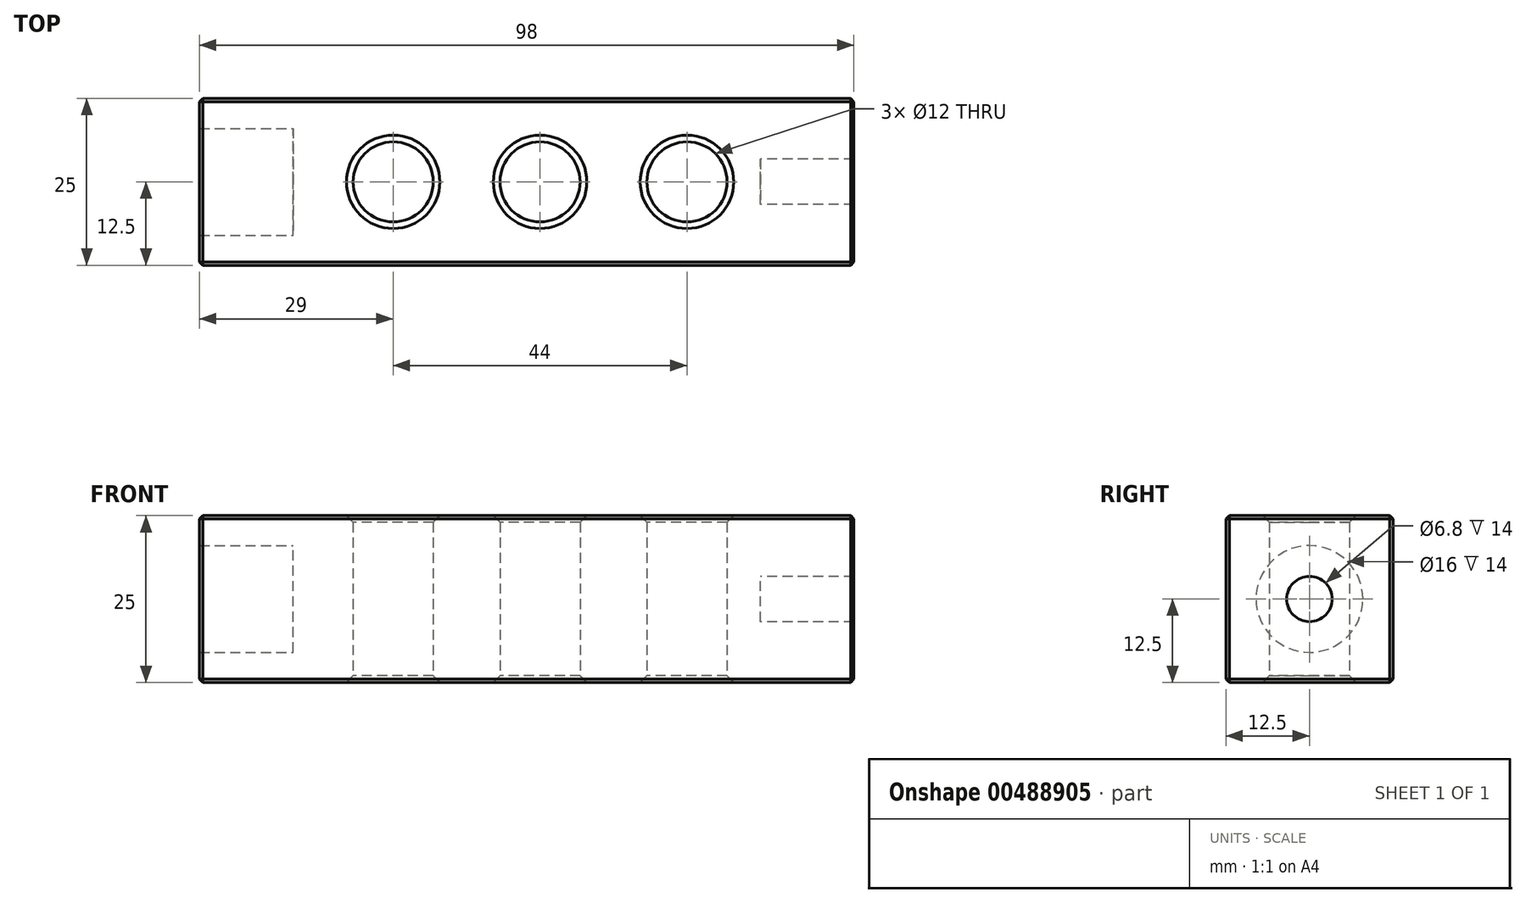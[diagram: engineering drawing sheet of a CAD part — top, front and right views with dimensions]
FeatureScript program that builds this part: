
annotation { "Feature Type Name" : "Feature", "Feature Type Description" : "" }
export const myFeature = defineFeature(function(context is Context, id is Id, definition is map)
    precondition{}
    {
        {
            var Q0;
            Q0=qCreatedBy(makeId("Top.planeOp"),FACE);
            var sketch = newSketch(context, id + "F0", { "sketchPlane" : qUnion([Q0])});
            skLineSegment(sketch, "E0.bottom", {"start": v(49, 12.5) * mm, "end": v(-49, 12.5) * mm});
            skLineSegment(sketch, "E0.top", {"start": v(49, -12.5) * mm, "end": v(-49, -12.5) * mm});
            skLineSegment(sketch, "E0.left", {"start": v(49, 12.5) * mm, "end": v(49, -12.5) * mm});
            skLineSegment(sketch, "E0.right", {"start": v(-49, 12.5) * mm, "end": v(-49, -12.5) * mm});
            skPoint(sketch, "E0.middle", {"position": v(0, 0) * mm});
            skLineSegment(sketch, "E1", {"start": v(49, 0) * mm, "end": v(-49, 0) * mm, "construction": true});
            skLineSegment(sketch, "E2", {"start": v(49, 12.5) * mm, "end": v(49, 22.83) * mm, "construction": true});
            skLineSegment(sketch, "E3", {"start": v(49, 22.83) * mm, "end": v(24, 22.83) * mm, "construction": true});
            skLineSegment(sketch, "E4", {"start": v(24, 22.83) * mm, "end": v(24, -3.88) * mm, "construction": true});
            skCircle(sketch, "E5", {"center": v(24, 0) * mm, "radius": 6 * mm});
            skCircle(sketch, "E6.1.0.0", {"center": v(2, 0) * mm, "radius": 6 * mm});
            skCircle(sketch, "E6.2.0.0", {"center": v(-20, 0) * mm, "radius": 6 * mm});
            skLineSegment(sketch, "E6.direction1", {"start": v(24, 0) * mm, "end": v(2, 0) * mm, "construction": true});
            skSolve(sketch);
        }
        {
            var Q0;
            Q0=makeQuery(id+"F0.imprint","IMPRINT",FACE,{"disambiguationData":[TD([[makeQuery(id+"F0.imprint","IMPRINT",EDGE,{"derivedFrom":sQuery(id+"F0.wireOp",EDGE,"E0.bottom")}),1.0]])]});
            extrude(context, id + "F1", {"entities" : qUnion([Q0]), "depth" : 25 * mm});
        }
        {
            var Q0;
            Q0=qCreatedBy(makeId("Right.planeOp"),FACE);
            var sketch = newSketch(context, id + "F2", { "sketchPlane" : qUnion([Q0])});
            skLineSegment(sketch, "E7", {"start": v(0, 0) * mm, "end": v(0, 12.5) * mm, "construction": true});
            skCircle(sketch, "E8", {"center": v(0, 12.5) * mm, "radius": 3.4 * mm});
            skSolve(sketch);
        }
        {
            var Q0;
            Q0 = qSketchRegion(id + "F2", true);
            extrude(context, id + "F3", {"entities" : qUnion([Q0]), "operationType" : NewBodyOperationType.REMOVE, "depth" : 120 * mm, "hasSecondDirection" : true, "secondDirectionOppositeDirection" : true, "secondDirectionDepth" : -35 * mm, "offsetDistance" : 25 * mm});
        }
        {
            var Q0;
            Q0=qCreatedBy(makeId("Top.planeOp"),FACE);
            cPlane(context, id + "F4", {"entities" : qUnion([Q0]), "cplaneType" : CPlaneType.OFFSET, "offset" : 12.5 * mm, "width" : 150 * mm, "height" : 150 * mm});
        }
        {
            var Q0;
            Q0=qCreatedBy(id+"F4.planeOp",FACE);
            var sketch = newSketch(context, id + "F5", { "sketchPlane" : qUnion([Q0])});
            skLineSegment(sketch, "E9", {"start": v(0, 0) * mm, "end": v(100, 0) * mm, "construction": true});
            skArc(sketch, "E10", {"start": v(112.5, 0) * mm, "mid": v(100, 12.5) * mm, "end": v(87.5, 0) * mm});
            skLineSegment(sketch, "E11", {"start": v(100, 0) * mm, "end": v(112.5, 0) * mm});
            skLineSegment(sketch, "E12", {"start": v(100, 0) * mm, "end": v(87.5, 0) * mm});
            skSolve(sketch);
        }
        {
            var Q0;
            Q0=qCreatedBy(makeId("Right.planeOp"),FACE);
            var sketch = newSketch(context, id + "F6", { "sketchPlane" : qUnion([Q0])});
            skLineSegment(sketch, "E13", {"start": v(0, 0) * mm, "end": v(0, 12.5) * mm, "construction": true});
            skCircle(sketch, "E14", {"center": v(0, 12.5) * mm, "radius": 8 * mm});
            skSolve(sketch);
        }
        {
            var Q0;
            Q0 = qSketchRegion(id + "F6", true);
            extrude(context, id + "F7", {"entities" : qUnion([Q0]), "operationType" : NewBodyOperationType.REMOVE, "oppositeDirection" : true, "depth" : 100 * mm, "hasSecondDirection" : true, "secondDirectionOppositeDirection" : true, "secondDirectionDepth" : 35 * mm, "offsetDistance" : 25 * mm});
        }
        {
            var Q0;
            Q0=makeQuery(id+"F1.opExtrude","SWEPT_EDGE",EDGE,{"disambiguationData":[OSD([sQuery(id+"F0.wireOp",EDGE,"E0.bottom"),sQuery(id+"F0.wireOp",EDGE,"E0.left")])]});
            var Q1;
            Q1=makeQuery(id+"F1.opExtrude","SWEPT_EDGE",EDGE,{"disambiguationData":[OSD([sQuery(id+"F0.wireOp",EDGE,"E0.top"),sQuery(id+"F0.wireOp",EDGE,"E0.left")])]});
            var Q2;
            Q2=makeQuery(id+"F1.opExtrude","CAP_EDGE",EDGE,{"disambiguationData":[OSD([sQuery(id+"F0.wireOp",EDGE,"E0.left")])],"isStart":true});
            var Q3;
            Q3=makeQuery(id+"F1.opExtrude","CAP_EDGE",EDGE,{"disambiguationData":[OSD([sQuery(id+"F0.wireOp",EDGE,"E0.left")])],"isStart":false});
            var Q4;
            Q4=makeQuery(id+"F1.opExtrude","CAP_EDGE",EDGE,{"disambiguationData":[OSD([sQuery(id+"F0.wireOp",EDGE,"E0.right")])],"isStart":false});
            var Q5;
            Q5=makeQuery(id+"F1.opExtrude","CAP_EDGE",EDGE,{"disambiguationData":[OSD([sQuery(id+"F0.wireOp",EDGE,"E0.bottom")])],"isStart":false});
            var Q6;
            Q6=makeQuery(id+"F1.opExtrude","CAP_EDGE",EDGE,{"disambiguationData":[OSD([sQuery(id+"F0.wireOp",EDGE,"E0.top")])],"isStart":false});
            var Q7;
            Q7=makeQuery(id+"F1.opExtrude","CAP_EDGE",EDGE,{"disambiguationData":[OSD([sQuery(id+"F0.wireOp",EDGE,"E0.top")])],"isStart":true});
            var Q8;
            Q8=makeQuery(id+"F1.opExtrude","SWEPT_EDGE",EDGE,{"disambiguationData":[OSD([sQuery(id+"F0.wireOp",EDGE,"E0.top"),sQuery(id+"F0.wireOp",EDGE,"E0.right")])]});
            var Q9;
            Q9=makeQuery(id+"F1.opExtrude","CAP_EDGE",EDGE,{"disambiguationData":[OSD([sQuery(id+"F0.wireOp",EDGE,"E0.right")])],"isStart":true});
            var Q10;
            Q10=makeQuery(id+"F1.opExtrude","SWEPT_EDGE",EDGE,{"disambiguationData":[OSD([sQuery(id+"F0.wireOp",EDGE,"E0.bottom"),sQuery(id+"F0.wireOp",EDGE,"E0.right")])]});
            var Q11;
            Q11=makeQuery(id+"F1.opExtrude","CAP_EDGE",EDGE,{"disambiguationData":[OSD([sQuery(id+"F0.wireOp",EDGE,"E0.bottom")])],"isStart":true});
            chamfer(context, id + "F8", {"entities" : qUnion([Q0, Q1, Q2, Q3, Q4, Q5, Q6, Q7, Q8, Q9, Q10, Q11]), "width" : .5 * mm, "tangentPropagation" : true});
        }
        {
            var Q0;
            Q0=makeQuery(id+"F1.opExtrude","CAP_EDGE",EDGE,{"disambiguationData":[OSD([sQuery(id+"F0.wireOp",EDGE,"E6.1.0.0")])],"isStart":true});
            var Q1;
            Q1=makeQuery(id+"F1.opExtrude","CAP_EDGE",EDGE,{"disambiguationData":[OSD([sQuery(id+"F0.wireOp",EDGE,"E5")])],"isStart":true});
            var Q2;
            Q2=makeQuery(id+"F1.opExtrude","CAP_EDGE",EDGE,{"disambiguationData":[OSD([sQuery(id+"F0.wireOp",EDGE,"E6.2.0.0")])],"isStart":true});
            var Q3;
            Q3=makeQuery(id+"F1.opExtrude","CAP_EDGE",EDGE,{"disambiguationData":[OSD([sQuery(id+"F0.wireOp",EDGE,"E6.2.0.0")])],"isStart":false});
            var Q4;
            Q4=makeQuery(id+"F1.opExtrude","CAP_EDGE",EDGE,{"disambiguationData":[OSD([sQuery(id+"F0.wireOp",EDGE,"E6.1.0.0")])],"isStart":false});
            var Q5;
            Q5=makeQuery(id+"F1.opExtrude","CAP_EDGE",EDGE,{"disambiguationData":[OSD([sQuery(id+"F0.wireOp",EDGE,"E5")])],"isStart":false});
            chamfer(context, id + "F9", {"entities" : qUnion([Q0, Q1, Q2, Q3, Q4, Q5]), "width" : 1 * mm, "tangentPropagation" : true});
        }
    });
